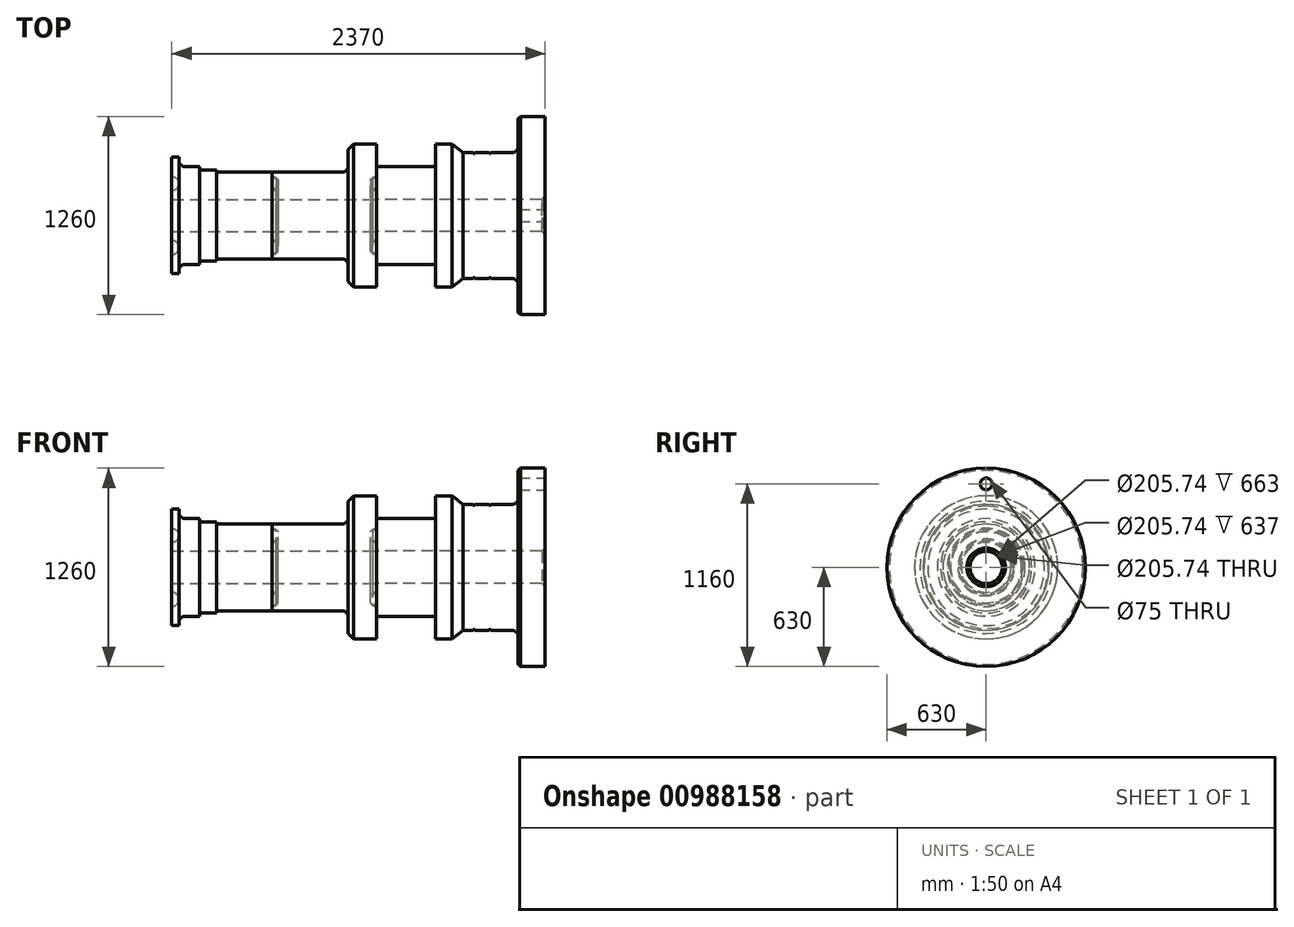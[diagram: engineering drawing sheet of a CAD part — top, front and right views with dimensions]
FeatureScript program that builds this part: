
annotation { "Feature Type Name" : "Feature", "Feature Type Description" : "" }
export const myFeature = defineFeature(function(context is Context, id is Id, definition is map)
    precondition{}
    {
        {
            var Q0;
            Q0=qCreatedBy(makeId("Top.planeOp"),FACE);
            var sketch = newSketch(context, id + "F0", { "sketchPlane" : qUnion([Q0])});
            skLineSegment(sketch, "E0", {"start": v(-1300.17, 0) * mm, "end": v(0, 0) * mm, "construction": true});
            skLineSegment(sketch, "E1", {"start": v(0, 102.87) * mm, "end": v(0, 630) * mm});
            skLineSegment(sketch, "E2", {"start": v(0, 630) * mm, "end": v(-170, 630) * mm});
            skLineSegment(sketch, "E3", {"start": v(-170, 630) * mm, "end": v(-170, 400) * mm});
            skLineSegment(sketch, "E4", {"start": v(-170, 400) * mm, "end": v(-342, 400) * mm});
            skLineSegment(sketch, "E5", {"start": v(-520, 400) * mm, "end": v(-590, 455) * mm});
            skLineSegment(sketch, "E6", {"start": v(-590, 455) * mm, "end": v(-695, 455) * mm});
            skLineSegment(sketch, "E7", {"start": v(-695, 455) * mm, "end": v(-695, 310) * mm});
            skLineSegment(sketch, "E8", {"start": v(-695, 310) * mm, "end": v(-1070, 310) * mm});
            skLineSegment(sketch, "E9", {"start": v(-1070, 310) * mm, "end": v(-1070, 240.87) * mm});
            skLineSegment(sketch, "E10", {"start": v(-1070, 102.87) * mm, "end": v(0, 102.87) * mm});
            skLineSegment(sketch, "E11", {"start": v(-458, 400) * mm, "end": v(-450, 392) * mm});
            skLineSegment(sketch, "E12", {"start": v(-450, 392) * mm, "end": v(-442, 400) * mm});
            skLineSegment(sketch, "E13", {"start": v(-358, 400) * mm, "end": v(-350, 392) * mm});
            skLineSegment(sketch, "E14", {"start": v(-350, 392) * mm, "end": v(-342, 400) * mm});
            skLineSegment(sketch, "E15", {"start": v(-450, 392) * mm, "end": v(-350, 392) * mm, "construction": true});
            skLineSegment(sketch, "E16.trimOffspring", {"start": v(-458, 400) * mm, "end": v(-520, 400) * mm});
            skLineSegment(sketch, "E17.trimOffspring", {"start": v(-358, 400) * mm, "end": v(-442, 400) * mm});
            skArc(sketch, "E18", {"start": v(-1070, 240.87) * mm, "mid": v(-1083.98, 238.2) * mm, "end": v(-1096, 230.58) * mm});
            skLineSegment(sketch, "E19", {"start": v(-1096, 230.58) * mm, "end": v(-1096, 175.16) * mm});
            skArc(sketch, "E20.trimOffspring", {"start": v(-1096, 175.16) * mm, "mid": v(-1083.98, 167.54) * mm, "end": v(-1070, 164.87) * mm});
            skLineSegment(sketch, "E21.trimOffspring", {"start": v(-1070, 164.87) * mm, "end": v(-1070, 102.87) * mm});
            skArc(sketch, "E22", {"start": v(-1070, 240.87) * mm, "mid": v(-1108, 202.87) * mm, "end": v(-1070, 164.87) * mm, "construction": true});
            skSolve(sketch);
        }
        {
            var Q0;
            Q0=qSketchRegion(id+"F0",true);
            var Q1;
            Q1=sQuery(id+"F0.wireOp",EDGE,"E0");
            revolve(context, id + "F1", {"surfaceOperationType" : NewSurfaceOperationType.NEW, "entities" : qUnion([Q0]), "axis" : qUnion([Q1]), "revolveType" : RevolveType.FULL});
        }
        {
            var Q0;
            Q0=makeQuery(id+"F1.opRevolve","SWEPT_EDGE",EDGE,{"disambiguationData":[OSD([sQuery(id+"F0.wireOp",EDGE,"E11"),sQuery(id+"F0.wireOp",EDGE,"E12")])]});
            var Q1;
            Q1=makeQuery(id+"F1.opRevolve","SWEPT_EDGE",EDGE,{"disambiguationData":[OSD([sQuery(id+"F0.wireOp",EDGE,"E13"),sQuery(id+"F0.wireOp",EDGE,"E14")])]});
            var Q2;
            Q2=makeQuery(id+"F1.opRevolve","SWEPT_EDGE",EDGE,{"disambiguationData":[OSD([sQuery(id+"F0.wireOp",EDGE,"E11"),sQuery(id+"F0.wireOp",EDGE,"E16.trimOffspring")])]});
            var Q3;
            Q3=makeQuery(id+"F1.opRevolve","SWEPT_EDGE",EDGE,{"disambiguationData":[OSD([sQuery(id+"F0.wireOp",EDGE,"E12"),sQuery(id+"F0.wireOp",EDGE,"E17.trimOffspring")])]});
            var Q4;
            Q4=makeQuery(id+"F1.opRevolve","SWEPT_EDGE",EDGE,{"disambiguationData":[OSD([sQuery(id+"F0.wireOp",EDGE,"E13"),sQuery(id+"F0.wireOp",EDGE,"E17.trimOffspring")])]});
            var Q5;
            Q5=makeQuery(id+"F1.opRevolve","SWEPT_EDGE",EDGE,{"disambiguationData":[OSD([sQuery(id+"F0.wireOp",EDGE,"E4"),sQuery(id+"F0.wireOp",EDGE,"E14")])]});
            fillet(context, id + "F2", {"entities" : qUnion([Q0, Q1, Q2, Q3, Q4, Q5]), "radius" : 5 * mm, "tangentPropagation" : true, "allowEdgeOverflow" : false});
        }
        {
            var Q0;
            Q0=makeQuery(id+"F1.opRevolve","SWEPT_EDGE",EDGE,{"disambiguationData":[OSD([sQuery(id+"F0.wireOp",EDGE,"E3"),sQuery(id+"F0.wireOp",EDGE,"E4")])]});
            fillet(context, id + "F3", {"entities" : qUnion([Q0]), "radius" : 40 * mm, "tangentPropagation" : true, "allowEdgeOverflow" : false});
        }
        {
            var Q0;
            Q0=makeQuery(id+"F1.opRevolve","SWEPT_EDGE",EDGE,{"disambiguationData":[OSD([sQuery(id+"F0.wireOp",EDGE,"E2"),sQuery(id+"F0.wireOp",EDGE,"E3")])]});
            chamfer(context, id + "F4", {"entities" : qUnion([Q0]), "width" : 15 * mm, "tangentPropagation" : true});
        }
        {
            var Q0;
            Q0=qCreatedBy(makeId("Top.planeOp"),FACE);
            var sketch = newSketch(context, id + "F5", { "sketchPlane" : qUnion([Q0])});
            skLineSegment(sketch, "E23.0", {"start": v(-1070, -310) * mm, "end": v(-1070, 157.87) * mm, "construction": true});
            skLineSegment(sketch, "E24", {"start": v(-1070, 0) * mm, "end": v(-1879.45, 0) * mm, "construction": true});
            skLineSegment(sketch, "E25", {"start": v(-1070, 102.87) * mm, "end": v(-1070, 157.87) * mm});
            skLineSegment(sketch, "E26", {"start": v(-1070, 455) * mm, "end": v(-1250, 455) * mm});
            skLineSegment(sketch, "E27", {"start": v(-1250, 455) * mm, "end": v(-1250, 275) * mm});
            skLineSegment(sketch, "E28", {"start": v(-1250, 275) * mm, "end": v(-1733, 275) * mm});
            skLineSegment(sketch, "E29", {"start": v(-1733, 275) * mm, "end": v(-1733, 247.87) * mm});
            skLineSegment(sketch, "E30", {"start": v(-1733, 102.87) * mm, "end": v(-1070, 102.87) * mm});
            skArc(sketch, "E31", {"start": v(-1733, 247.87) * mm, "mid": v(-1710.47, 241.83) * mm, "end": v(-1694, 225.32) * mm});
            skLineSegment(sketch, "E32", {"start": v(-1694, 225.32) * mm, "end": v(-1694, 180.42) * mm});
            skArc(sketch, "E33.trimOffspring", {"start": v(-1694, 180.42) * mm, "mid": v(-1710.47, 163.91) * mm, "end": v(-1733, 157.87) * mm});
            skLineSegment(sketch, "E34.trimOffspring", {"start": v(-1733, 157.87) * mm, "end": v(-1733, 102.87) * mm});
            skArc(sketch, "E35", {"start": v(-1733, 247.87) * mm, "mid": v(-1688, 202.87) * mm, "end": v(-1733, 157.87) * mm, "construction": true});
            skLineSegment(sketch, "E36.trimOffspring", {"start": v(-1070, 247.87) * mm, "end": v(-1070, 310) * mm, "construction": true});
            skLineSegment(sketch, "E37.trimOffspring", {"start": v(-1070, 247.87) * mm, "end": v(-1070, 455) * mm});
            skArc(sketch, "E38", {"start": v(-1070, 247.87) * mm, "mid": v(-1092.53, 241.83) * mm, "end": v(-1109, 225.32) * mm});
            skLineSegment(sketch, "E39", {"start": v(-1109, 225.32) * mm, "end": v(-1109, 180.42) * mm});
            skArc(sketch, "E40.trimOffspring", {"start": v(-1109, 180.42) * mm, "mid": v(-1092.53, 163.91) * mm, "end": v(-1070, 157.87) * mm});
            skArc(sketch, "E41", {"start": v(-1070, 247.87) * mm, "mid": v(-1115, 202.87) * mm, "end": v(-1070, 157.87) * mm, "construction": true});
            skSolve(sketch);
        }
        {
            var Q0;
            Q0=makeQuery(id+"F5.imprint","IMPRINT",FACE,{"disambiguationData":[TD([[makeQuery(id+"F5.imprint","IMPRINT",EDGE,{"derivedFrom":sQuery(id+"F5.wireOp",EDGE,"E25")}),1.0]])]});
            var Q1;
            Q1=sQuery(id+"F5.wireOp",EDGE,"E24");
            revolve(context, id + "F6", {"surfaceOperationType" : NewSurfaceOperationType.NEW, "entities" : qUnion([Q0]), "axis" : qUnion([Q1]), "revolveType" : RevolveType.FULL});
        }
        {
            var Q0;
            Q0=makeQuery(id+"F6.opRevolve","SWEPT_EDGE",EDGE,{"disambiguationData":[OSD([sQuery(id+"F5.wireOp",EDGE,"E27"),sQuery(id+"F5.wireOp",EDGE,"E28")])]});
            fillet(context, id + "F7", {"entities" : qUnion([Q0]), "radius" : 40 * mm, "tangentPropagation" : true, "allowEdgeOverflow" : false});
        }
        {
            var Q0;
            Q0=makeQuery(id+"F6.opRevolve","SWEPT_EDGE",EDGE,{"disambiguationData":[OSD([sQuery(id+"F5.wireOp",EDGE,"E26"),sQuery(id+"F5.wireOp",EDGE,"E27")])]});
            chamfer(context, id + "F8", {"entities" : qUnion([Q0]), "width" : 35 * mm, "tangentPropagation" : true});
        }
        {
            var Q0;
            Q0=qCreatedBy(makeId("Top.planeOp"),FACE);
            var sketch = newSketch(context, id + "F9", { "sketchPlane" : qUnion([Q0])});
            skLineSegment(sketch, "E42.0", {"start": v(-1733, 275) * mm, "end": v(-1733, 240.87) * mm, "construction": true});
            skLineSegment(sketch, "E43", {"start": v(-1733, 102.87) * mm, "end": v(-1733, 164.87) * mm});
            skLineSegment(sketch, "E44", {"start": v(-2085, 275) * mm, "end": v(-2085, 290) * mm});
            skLineSegment(sketch, "E45", {"start": v(-2085, 290) * mm, "end": v(-2195, 290) * mm});
            skLineSegment(sketch, "E46", {"start": v(-2195, 290) * mm, "end": v(-2195, 310) * mm});
            skLineSegment(sketch, "E47", {"start": v(-2195, 310) * mm, "end": v(-2325, 310) * mm});
            skLineSegment(sketch, "E48", {"start": v(-2325, 310) * mm, "end": v(-2325, 370) * mm});
            skLineSegment(sketch, "E49", {"start": v(-2325, 370) * mm, "end": v(-2370, 370) * mm});
            skLineSegment(sketch, "E50", {"start": v(-2370, 370) * mm, "end": v(-2370, 247.87) * mm});
            skLineSegment(sketch, "E51", {"start": v(-2085, 275) * mm, "end": v(-1733, 275) * mm});
            skLineSegment(sketch, "E52", {"start": v(-1733, 102.87) * mm, "end": v(-2370, 102.87) * mm});
            skPoint(sketch, "E53", {"position": v(-1733, 0) * mm});
            skLineSegment(sketch, "E54", {"start": v(-1733, 0) * mm, "end": v(-2718.15, 0) * mm, "construction": true});
            skArc(sketch, "E55", {"start": v(-2370, 247.87) * mm, "mid": v(-2347.47, 241.83) * mm, "end": v(-2331, 225.32) * mm});
            skLineSegment(sketch, "E56", {"start": v(-2331, 225.32) * mm, "end": v(-2331, 180.42) * mm});
            skLineSegment(sketch, "E57.trimOffspring", {"start": v(-2370, 157.87) * mm, "end": v(-2370, 102.87) * mm});
            skArc(sketch, "E58.trimOffspring", {"start": v(-2331, 180.42) * mm, "mid": v(-2347.47, 163.91) * mm, "end": v(-2370, 157.87) * mm});
            skArc(sketch, "E59", {"start": v(-2370, 247.87) * mm, "mid": v(-2325, 202.87) * mm, "end": v(-2370, 157.87) * mm, "construction": true});
            skArc(sketch, "E60", {"start": v(-1733, 240.87) * mm, "mid": v(-1719.02, 238.2) * mm, "end": v(-1707, 230.58) * mm});
            skLineSegment(sketch, "E61", {"start": v(-1707, 230.58) * mm, "end": v(-1707, 175.16) * mm});
            skArc(sketch, "E62.trimOffspring", {"start": v(-1707, 175.16) * mm, "mid": v(-1719.02, 167.54) * mm, "end": v(-1733, 164.87) * mm});
            skLineSegment(sketch, "E63.trimOffspring", {"start": v(-1733, 164.87) * mm, "end": v(-1733, -275) * mm, "construction": true});
            skArc(sketch, "E64", {"start": v(-1733, 240.87) * mm, "mid": v(-1695, 202.87) * mm, "end": v(-1733, 164.87) * mm, "construction": true});
            skLineSegment(sketch, "E65.trimOffspring", {"start": v(-1733, 240.87) * mm, "end": v(-1733, 275) * mm});
            skSolve(sketch);
        }
        {
            var Q0;
            Q0=makeQuery(id+"F9.imprint","IMPRINT",FACE,{"disambiguationData":[TD([[makeQuery(id+"F9.imprint","IMPRINT",EDGE,{"derivedFrom":sQuery(id+"F9.wireOp",EDGE,"E43")}),1.0]])]});
            var Q1;
            Q1=sQuery(id+"F9.wireOp",EDGE,"E54");
            revolve(context, id + "F10", {"surfaceOperationType" : NewSurfaceOperationType.NEW, "entities" : qUnion([Q0]), "axis" : qUnion([Q1]), "revolveType" : RevolveType.FULL});
        }
        {
            var Q0;
            Q0=makeQuery(id+"F10.opRevolve","SWEPT_EDGE",EDGE,{"disambiguationData":[OSD([sQuery(id+"F9.wireOp",EDGE,"E47"),sQuery(id+"F9.wireOp",EDGE,"E48")])]});
            fillet(context, id + "F11", {"entities" : qUnion([Q0]), "radius" : 40 * mm, "tangentPropagation" : true, "allowEdgeOverflow" : false});
        }
        {
            var Q0;
            Q0=makeQuery(id+"F10.opRevolve","SWEPT_EDGE",EDGE,{"disambiguationData":[OSD([sQuery(id+"F9.wireOp",EDGE,"E45"),sQuery(id+"F9.wireOp",EDGE,"E46")])]});
            var Q1;
            Q1=makeQuery(id+"F10.opRevolve","SWEPT_EDGE",EDGE,{"disambiguationData":[OSD([sQuery(id+"F9.wireOp",EDGE,"E44"),sQuery(id+"F9.wireOp",EDGE,"E51")])]});
            fillet(context, id + "F12", {"entities" : qUnion([Q0, Q1]), "radius" : 10 * mm, "tangentPropagation" : true, "allowEdgeOverflow" : false});
        }
        {
            var Q0;
            Q0=makeQuery(id+"F1.opRevolve","SWEPT_FACE",FACE,{"disambiguationData":[OSD([sQuery(id+"F0.wireOp",EDGE,"E1")])]});
            var sketch = newSketch(context, id + "F13", { "sketchPlane" : qUnion([Q0])});
            skCircle(sketch, "E66", {"center": v(0, 0) * mm, "radius": 530 * mm, "construction": true});
            skLineSegment(sketch, "E67", {"start": v(0, 0) * mm, "end": v(0, 530) * mm, "construction": true});
            skCircle(sketch, "E68", {"center": v(0, 530) * mm, "radius": 37.5 * mm});
            skSolve(sketch);
        }
        {
            var Q0;
            Q0=makeQuery(id+"F13.imprint","IMPRINT",FACE,{"disambiguationData":[TD([[makeQuery(id+"F13.imprint","IMPRINT",EDGE,{"derivedFrom":sQuery(id+"F13.wireOp",EDGE,"E68")}),1.0]])]});
            extrude(context, id + "F14", {"entities" : qUnion([Q0]), "operationType" : NewBodyOperationType.REMOVE, "endBound" : BoundingType.UP_TO_NEXT, "oppositeDirection" : true, "depth" : 25 * mm, "offsetDistance" : 25 * mm});
        }
        {
            var Q0;
            Q0=makeQuery(id+"F1.opRevolve","SWEPT_EDGE",EDGE,{"disambiguationData":[OSD([sQuery(id+"F0.wireOp",EDGE,"E1"),sQuery(id+"F0.wireOp",EDGE,"E10")])]});
            chamfer(context, id + "F15", {"entities" : qUnion([Q0]), "width" : 20 * mm, "tangentPropagation" : true});
        }
    });
